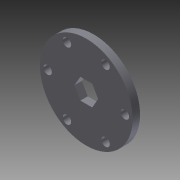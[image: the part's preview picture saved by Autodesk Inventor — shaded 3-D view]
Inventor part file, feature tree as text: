
AUTODESK INVENTOR PART (.ipt)
format: ipt  version: 2014 SP1 (Build 180222100, 222)  size: 98,816 bytes
history: native  units: in
note: dims shown in document units (in); Inventor stores cm internally (conversion verified against a paired STEP export)
features: extrude x1, sketch x1
ambient origin geometry x8: Origin, YZ Plane, XZ Plane, XY Plane, X Axis, Y Axis, Z Axis, Center Point
bodies: Solid1 (feature_tree)
feature tree (2):
  extrude  "Extrusion1"  Depth=0.18in
  sketch  "Sketch1"  dims[d0=2.25in d1=0.204in d2=0.5in d3=0.9375in d4=2.3622in d6=360.0deg d8=0.18in d9=0.0in]
